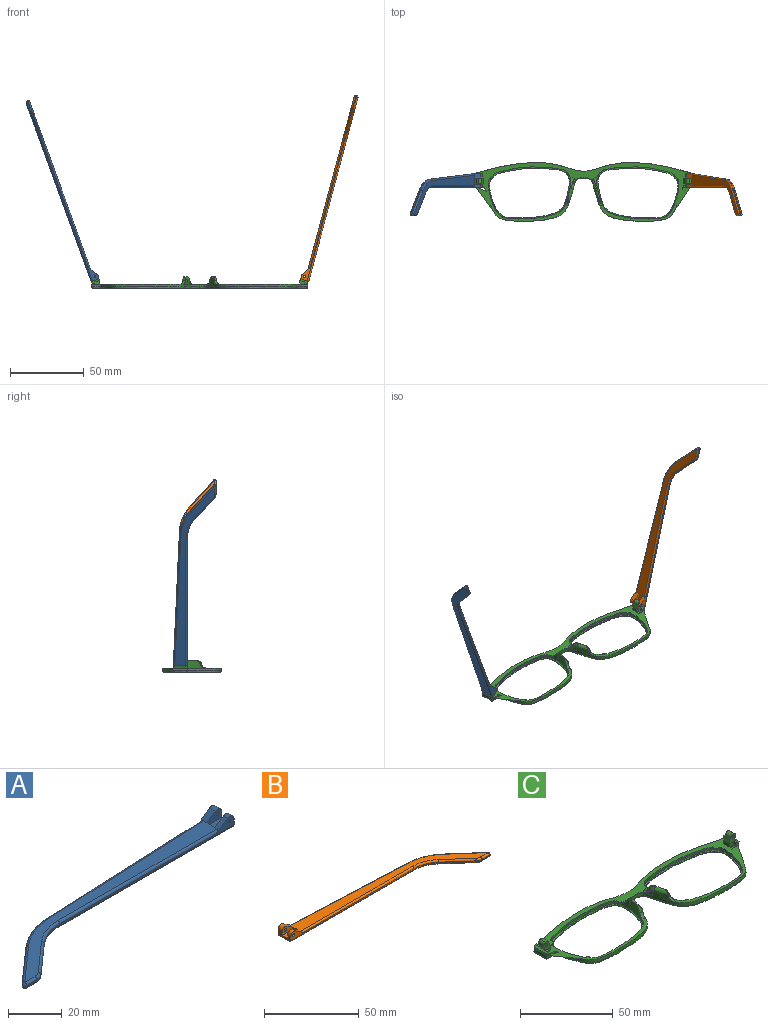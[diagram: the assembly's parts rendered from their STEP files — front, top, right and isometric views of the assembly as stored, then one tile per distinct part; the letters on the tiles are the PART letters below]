
ASSEMBLY  parts=3 mates=2
PART A: 43 faces, bbox 130.2x29.5x5.9 mm
  f0: plane 9.62x3.72mm, normal (1,0,0), area 24.7mm2, adj f1,f3,f4,f5,f10,f16,f18,f28
  f1: cylinder r=2.2mm len=3.45mm, axis (0,-1,0), area 11mm2, adj f0,f2,f4,f37
  f2: plane 6.01x3.91mm, normal (-0.55,0,0.84), area 12.7mm2, adj f1,f4,f9,f19,f37
  f3: plane 2.26x0.1mm, normal (0,0,1), area 0.1mm2, adj f0,f5,f18
  f4: plane 92.1x4.9mm, normal (0,-1,0), area 79.9mm2, adj f0,f1,f2,f14,f19,f36,f42
  f5: plane 93.42x4.13mm, normal (-0.04,1,0), area 64.8mm2, adj f0,f3,f11,f15,f17,f27,f28
  f6: plane 17.82x15.72mm, normal (-0.66,0.75,0), area 14.3mm2, adj f11,f12,f25,f30
  f7: plane 5.46x0.6mm, normal (0,-1,0), area 3.3mm2, adj f12,f13,f23,f32
  f8: plane 14.99x13.23mm, normal (0.66,-0.75,0), area 12mm2, adj f13,f14,f21,f34
  f9: plane 121.18x26.73mm, normal (0,0,1), area 627.7mm2, adj f2,f17,f19,f20,f21,f22,f23,f25
  f10: plane 129.1x27.08mm, normal (0,0,-1), area 686.5mm2, adj f0,f28,f29,f30,f32,f33,f34,f35
  f11: cylinder r=30mm len=18.52mm, axis (0,0,-1), area 12.2mm2, adj f5,f6,f26,f29
  f12: cylinder r=1mm len=1.75mm, axis (0,0,-1), area 1.5mm2, adj f6,f7,f24,f31
  f13: cylinder r=5mm len=3.31mm, axis (0,0,-1), area 2.2mm2, adj f7,f8,f22,f33
  f14: cylinder r=20mm len=13.23mm, axis (0,0,1), area 8.7mm2, adj f4,f8,f20,f35
  f15: plane 5.66x0.25mm, normal (0,0,-1), area 0.7mm2, adj f5,f17,f18
  f16: cylinder r=2.2mm len=3.45mm, axis (0,-1,0), area 14.8mm2, adj f0,f17,f18,f38
  f17: plane 6.01x3.91mm, normal (-0.55,0,0.84), area 16.9mm2, adj f5,f9,f15,f16,f18,f27,f38
  f18: plane 7.92x3.3mm, normal (0,1,0), area 15.9mm2, adj f0,f3,f15,f16,f17,f41
  f19: cylinder r=1mm len=84.18mm, axis (-1,0,0), area 131.4mm2, adj f2,f4,f9,f20
  f20: torus R=21mm, axis (0,0,1), area 23.1mm2, adj f9,f14,f19,f21
  f21: cylinder r=1mm len=15.65mm, axis (-0.75,-0.66,0), area 31.4mm2, adj f8,f9,f20,f22
  f22: torus R=4mm, axis (0,0,1), area 5.3mm2, adj f9,f13,f21,f23
  f23: cylinder r=1mm len=5.46mm, axis (-1,0,0), area 8.6mm2, adj f7,f9,f22,f24
  f24: sphere r=1mm, area 2.4mm2, adj f12,f23,f25
  f25: cylinder r=1mm len=18.48mm, axis (0.75,0.66,0), area 37.3mm2, adj f6,f9,f24,f26
  f26: torus R=29mm, axis (0,0,1), area 31.6mm2, adj f9,f11,f25,f27
  f27: cylinder r=1mm len=85.5mm, axis (1,0.04,0), area 133.5mm2, adj f5,f9,f17,f26
  f28: cylinder r=1mm len=93.46mm, axis (-1,-0.04,0), area 146.9mm2, adj f0,f5,f10,f29
  f29: torus R=29mm, axis (0,0,1), area 31.6mm2, adj f10,f11,f28,f30
  f30: cylinder r=1mm len=18.48mm, axis (-0.75,-0.66,0), area 37.3mm2, adj f6,f10,f29,f31
  f31: sphere r=1mm, area 2.4mm2, adj f12,f30,f32
  f32: cylinder r=1mm len=5.46mm, axis (1,0,0), area 8.6mm2, adj f7,f10,f31,f33
  f33: torus R=4mm, axis (0,0,1), area 5.3mm2, adj f10,f13,f32,f34
  f34: cylinder r=1mm len=15.65mm, axis (0.75,0.66,0), area 31.4mm2, adj f8,f10,f33,f35
  f35: torus R=21mm, axis (0,0,1), area 23.1mm2, adj f10,f14,f34,f36
  f36: cylinder r=1mm len=92.1mm, axis (1,0,0), area 144.7mm2, adj f0,f4,f10,f35
  f37: plane 7.92x4.7mm, normal (0,1,0), area 27mm2, adj f0,f1,f2,f39,f40,f42
  f38: plane 7.92x4.7mm, normal (0,-1,0), area 27mm2, adj f0,f16,f17,f39,f40,f41
  f39: plane 7.92x4.1mm, normal (0,0,1), area 32.5mm2, adj f0,f37,f38,f40
  f40: plane 4.1x1.4mm, normal (1,0,0), area 5.7mm2, adj f9,f37,f38,f39
  f41: cylinder r=0.5mm len=3.1mm, axis (0,-1,0), area 9.7mm2, adj f18,f38
  f42: cylinder r=0.5mm len=2.3mm, axis (0,-1,0), area 7.2mm2, adj f4,f37
PART B: 43 faces, bbox 130.2x29.5x5.9 mm
  f0: plane 9.62x3.72mm, normal (-1,0,0), area 24.7mm2, adj f1,f3,f4,f5,f10,f16,f18,f28
  f1: cylinder r=2.2mm len=3.45mm, axis (0,-1,0), area 11mm2, adj f0,f2,f4,f37
  f2: plane 6.01x3.91mm, normal (0.55,0,0.84), area 12.7mm2, adj f1,f4,f9,f19,f37
  f3: plane 2.26x0.1mm, normal (0,0,1), area 0.1mm2, adj f0,f5,f18
  f4: plane 92.1x4.9mm, normal (0,-1,0), area 78.2mm2, adj f0,f1,f2,f14,f19,f36,f42
  f5: plane 93.42x4.13mm, normal (0.04,1,0), area 64.8mm2, adj f0,f3,f11,f15,f17,f27,f28
  f6: plane 17.82x15.72mm, normal (0.66,0.75,0), area 14.3mm2, adj f11,f12,f25,f30
  f7: plane 5.46x0.6mm, normal (0,-1,0), area 3.3mm2, adj f12,f13,f23,f32
  f8: plane 14.99x13.23mm, normal (-0.66,-0.75,0), area 12mm2, adj f13,f14,f21,f34
  f9: plane 121.18x26.73mm, normal (0,0,1), area 627.7mm2, adj f2,f17,f19,f20,f21,f22,f23,f25
  f10: plane 129.1x27.08mm, normal (0,0,-1), area 686.5mm2, adj f0,f28,f29,f30,f32,f33,f34,f35
  f11: cylinder r=30mm len=18.52mm, axis (0,0,-1), area 12.2mm2, adj f5,f6,f26,f29
  f12: cylinder r=1mm len=1.75mm, axis (0,0,-1), area 1.5mm2, adj f6,f7,f24,f31
  f13: cylinder r=5mm len=3.31mm, axis (0,0,-1), area 2.2mm2, adj f7,f8,f22,f33
  f14: cylinder r=20mm len=13.23mm, axis (0,0,1), area 8.7mm2, adj f4,f8,f20,f35
  f15: plane 5.66x0.25mm, normal (0,0,-1), area 0.7mm2, adj f5,f17,f18
  f16: cylinder r=2.2mm len=3.45mm, axis (0,-1,0), area 14.8mm2, adj f0,f17,f18,f38
  f17: plane 6.01x3.91mm, normal (0.55,0,0.84), area 16.9mm2, adj f5,f9,f15,f16,f18,f27,f38
  f18: plane 7.92x3.3mm, normal (0,1,0), area 14.3mm2, adj f0,f3,f15,f16,f17,f41
  f19: cylinder r=1mm len=84.18mm, axis (1,0,0), area 131.4mm2, adj f2,f4,f9,f20
  f20: torus R=21mm, axis (0,0,1), area 23.1mm2, adj f9,f14,f19,f21
  f21: cylinder r=1mm len=15.65mm, axis (0.75,-0.66,0), area 31.4mm2, adj f8,f9,f20,f22
  f22: torus R=4mm, axis (0,0,1), area 5.3mm2, adj f9,f13,f21,f23
  f23: cylinder r=1mm len=5.46mm, axis (1,0,0), area 8.6mm2, adj f7,f9,f22,f24
  f24: sphere r=1mm, area 2.4mm2, adj f12,f23,f25
  f25: cylinder r=1mm len=18.48mm, axis (-0.75,0.66,0), area 37.3mm2, adj f6,f9,f24,f26
  f26: torus R=29mm, axis (0,0,1), area 31.6mm2, adj f9,f11,f25,f27
  f27: cylinder r=1mm len=85.5mm, axis (-1,0.04,0), area 133.5mm2, adj f5,f9,f17,f26
  f28: cylinder r=1mm len=93.46mm, axis (1,-0.04,0), area 146.9mm2, adj f0,f5,f10,f29
  f29: torus R=29mm, axis (0,0,1), area 31.6mm2, adj f10,f11,f28,f30
  f30: cylinder r=1mm len=18.48mm, axis (0.75,-0.66,0), area 37.3mm2, adj f6,f10,f29,f31
  f31: sphere r=1mm, area 2.4mm2, adj f12,f30,f32
  f32: cylinder r=1mm len=5.46mm, axis (-1,0,0), area 8.6mm2, adj f7,f10,f31,f33
  f33: torus R=4mm, axis (0,0,1), area 5.3mm2, adj f10,f13,f32,f34
  f34: cylinder r=1mm len=15.65mm, axis (-0.75,0.66,0), area 31.4mm2, adj f8,f10,f33,f35
  f35: torus R=21mm, axis (0,0,1), area 23.1mm2, adj f10,f14,f34,f36
  f36: cylinder r=1mm len=92.1mm, axis (-1,0,0), area 144.7mm2, adj f0,f4,f10,f35
  f37: plane 7.92x4.7mm, normal (0,1,0), area 25.4mm2, adj f0,f1,f2,f39,f40,f42
  f38: plane 7.92x4.7mm, normal (0,-1,0), area 25.4mm2, adj f0,f16,f17,f39,f40,f41
  f39: plane 7.92x4.1mm, normal (0,0,1), area 32.5mm2, adj f0,f37,f38,f40
  f40: plane 4.1x1.4mm, normal (-1,0,0), area 5.7mm2, adj f9,f37,f38,f39
  f41: cylinder r=0.88mm len=3.1mm, axis (0,-1,0), area 17mm2, adj f18,f38
  f42: cylinder r=0.88mm len=2.3mm, axis (0,-1,0), area 12.6mm2, adj f4,f37
PART C: 118 faces, bbox 148.1x41x17.9 mm
  f0: bspline ~1.82x1.22mm, area 0.7mm2, adj f1,f114,f116,f117
  f1: bspline ~2.66x2.04mm, area 1.9mm2, adj f0,f2,f113,f114,f117
  f2: bspline ~3.55x3.47mm, area 3.7mm2, adj f1,f3,f112,f113,f117
  f3: plane 147.69x40.6mm, normal (0,0,1), area 854.2mm2, adj f2,f4,f16,f17,f18,f19,f20,f21
  f4: plane 1.23x0.04mm, normal (0,0,1), area 0mm2, adj f3,f5,f114
  f5: plane 2.76x2.53mm, normal (0,-1,0), area 3.9mm2, adj f4,f6,f15,f16,f24
  f6: plane 9.65x1.24mm, normal (0,0,1), area 8.2mm2, adj f5,f7,f14,f15,f19,f20,f21,f24
  f7: plane 5.77x5.06mm, normal (0,-1,0), area 17mm2, adj f6,f8,f9,f11,f12,f13,f14,f23
  f8: cylinder r=1.98mm len=4mm, axis (0,-1,0), area 12.4mm2, adj f7,f12,f14,f21
  f9: plane 4x3.31mm, normal (-0.94,0,0.34), area 14.1mm2, adj f7,f10,f11,f21
  f10: plane 4x0.02mm, normal (0.34,0,0.94), area 0.1mm2, adj f9,f21,f22
  f11: cylinder r=1.98mm len=4mm, axis (0,1,0), area 12.4mm2, adj f7,f9,f12,f21
  f12: plane 4x0.01mm, normal (0.34,0,0.94), area 0mm2, adj f7,f8,f11,f21
  f13: cylinder r=0.88mm len=4mm, axis (0,-1,0), area 22mm2, adj f7,f21
  f14: plane 4x2.21mm, normal (0.94,0,-0.34), area 9.4mm2, adj f6,f7,f8,f21
  f15: plane 9.71x1.44mm, normal (0.34,0,0.94), area 13.9mm2, adj f5,f6,f16,f17,f18,f19
  f16: cone r=1mm half-angle=20deg, axis (0,0,1), area 2.3mm2, adj f3,f5,f15,f17
  f17: plane 7.67x1.6mm, normal (0.94,0,-0.34), area 13mm2, adj f3,f15,f16,f18
  f18: cylinder r=1mm len=2.28mm, axis (-0.34,0,-0.94), area 3mm2, adj f3,f15,f17,f19
  f19: plane 2.1x1.69mm, normal (0,1,0), area 2.8mm2, adj f3,f6,f15,f18,f20
  f20: plane 3.3x2.1mm, normal (-1,0,0), area 6.9mm2, adj f3,f6,f19,f21
  f21: plane 6.97x5.07mm, normal (0,1,0), area 22.7mm2, adj f3,f6,f8,f9,f10,f11,f12,f13
  f22: plane 4x2.36mm, normal (-1,0,0), area 9.5mm2, adj f3,f10,f21,f23
  f23: plane 3.2x2.36mm, normal (0,-1,0), area 5.7mm2, adj f3,f7,f22,f24
  f24: plane 2.35x2.1mm, normal (-1,0,0), area 4.9mm2, adj f3,f5,f6,f7,f23
  f25: bspline ~3.7x3.66mm, area 7.8mm2, adj f3,f26,f31,f39,f114
  f26: bspline ~7.26x7.26mm, area 6.3mm2, adj f25,f27,f31,f39
  f27: bspline ~10.27x4.83mm, area 21.4mm2, adj f26,f28,f31,f39,f114,f117
  f28: plane 3.63x0.97mm, normal (0,0,1), area 0.3mm2, adj f27,f29,f39
  f29: bspline ~15.5x15.35mm, area 6.4mm2, adj f28,f30,f39,f112,f117
  f30: extruded ~4.98x1.37mm, area 6.6mm2, adj f29,f39
  f31: extruded ~4.44x3.32mm, area 15.1mm2, adj f25,f26,f27,f32,f114
  f32: plane 4.46x1.45mm, normal (0,0,1), area 0.1mm2, adj f31,f114
  f33: cylinder r=1.3mm len=1.78mm, axis (0,0,1), area 1.3mm2, adj f3,f34,f39
  f34: plane 1.79x1.31mm, normal (0,0,-1), area 0.9mm2, adj f33,f39
  f35: cylinder r=1.3mm len=1.93mm, axis (0,0,1), area 1.5mm2, adj f3,f36,f39
  f36: plane 1.95x1.68mm, normal (0,0,-1), area 1.5mm2, adj f35,f39
  f37: cylinder r=2.28mm len=3.13mm, axis (0,0,1), area 2.5mm2, adj f3,f38,f39
  f38: plane 3.14x2.79mm, normal (0,0,-1), area 3.9mm2, adj f37,f39
  f39: extruded ~55.69x35.36mm, area 226.3mm2, adj f3,f25,f26,f27,f28,f29,f30,f33
  f40: extruded ~55.69x35.36mm, area 160.5mm2, adj f39,f41
  f41: plane 56.06x35.45mm, normal (0,0,1), area 126.1mm2, adj f40,f42
  f42: bspline ~56.14x35.88mm, area 235.6mm2, adj f41,f43,f58
  f43: bspline ~72.96x30.43mm, area 161.5mm2, adj f42,f44,f57,f58,f114
  f44: bspline ~72.96x30.43mm, area 161.5mm2, adj f43,f45,f48,f58,f109
  f45: bspline ~56.14x35.88mm, area 235.6mm2, adj f44,f46,f58
  f46: plane 56.06x35.45mm, normal (0,0,1), area 126.1mm2, adj f45,f47
  f47: extruded ~55.69x35.36mm, area 160.5mm2, adj f46,f86
  f48: bspline ~1x1mm, area 0.8mm2, adj f44,f49,f109
  f49: bspline ~8.97x1.23mm, area 12.6mm2, adj f48,f50,f58,f109
  f50: bspline ~1.04x1mm, area 0.7mm2, adj f49,f51,f109
  f51: bspline ~45.82x8.59mm, area 59.8mm2, adj f50,f52,f58,f109
  f52: bspline ~37.02x6.7mm, area 56.6mm2, adj f51,f53,f58,f110
  f53: bspline ~37.02x6.7mm, area 56.6mm2, adj f52,f54,f58,f111
  f54: bspline ~45.82x8.59mm, area 59.8mm2, adj f53,f55,f58,f114
  f55: bspline ~1.04x1mm, area 0.8mm2, adj f54,f56,f114
  f56: bspline ~8.97x1.23mm, area 12.6mm2, adj f55,f57,f58,f114
  f57: bspline ~1x1mm, area 0.8mm2, adj f43,f56,f114
  f58: plane 144.78x37.9mm, normal (0,0,-1), area 565.6mm2, adj f42,f43,f44,f45,f49,f51,f52,f53
  f59: plane 3.19x1.37mm, normal (0,0,-1), area 2.1mm2, adj f39,f60
  f60: cylinder r=2.28mm len=3.17mm, axis (0,0,1), area 2.1mm2, adj f3,f39,f59,f112
  f61: bspline ~6.38x2.14mm, area 2.6mm2, adj f3,f62,f113,f114
  f62: bspline ~6.38x2.14mm, area 2.6mm2, adj f3,f61,f63,f109
  f63: bspline ~2.1x1.46mm, area 0.6mm2, adj f62,f64,f76,f109
  f64: bspline ~2.65x2.03mm, area 1.9mm2, adj f63,f65,f68,f76,f109
  f65: bspline ~2.19x1.4mm, area 0.7mm2, adj f64,f66,f68,f109
  f66: extruded ~3.67x3.11mm, area 5.9mm2, adj f65,f67,f68,f109
  f67: bspline ~5.24x1.75mm, area 0mm2, adj f66,f109
  f68: bspline ~6.1x4.93mm, area 12.6mm2, adj f64,f65,f66,f69,f74,f76,f109
  f69: bspline ~10.27x4.83mm, area 21.5mm2, adj f68,f70,f71,f73,f86,f109
  f70: plane 3.63x0.97mm, normal (0,0,1), area 0.3mm2, adj f69,f74,f86
  f71: extruded ~4.44x3.32mm, area 15.1mm2, adj f69,f72,f73,f87,f109
  f72: plane 4.46x1.45mm, normal (0,0,1), area 0.1mm2, adj f71,f109
  f73: bspline ~7.26x7.26mm, area 6.2mm2, adj f69,f71,f86,f87
  f74: bspline ~15.5x15.35mm, area 6.4mm2, adj f68,f70,f75,f77,f86
  f75: extruded ~4.98x1.36mm, area 6.6mm2, adj f74,f86
  f76: bspline ~3.55x3.47mm, area 3.7mm2, adj f3,f63,f64,f68,f77
  f77: bspline ~5.94x4.42mm, area 7.9mm2, adj f3,f74,f76,f78,f86
  f78: cylinder r=2.28mm len=3.17mm, axis (0,0,1), area 2.1mm2, adj f3,f77,f79,f86
  f79: plane 3.19x1.37mm, normal (0,0,-1), area 2.1mm2, adj f78,f86
  f80: cylinder r=2.28mm len=3.13mm, axis (0,0,1), area 2.5mm2, adj f3,f81,f86
  f81: plane 3.14x2.79mm, normal (0,0,-1), area 3.9mm2, adj f80,f86
  f82: cylinder r=1.3mm len=1.93mm, axis (0,0,1), area 1.5mm2, adj f3,f83,f86
  f83: plane 1.95x1.68mm, normal (0,0,-1), area 1.5mm2, adj f82,f86
  f84: cylinder r=1.3mm len=1.78mm, axis (0,0,1), area 1.3mm2, adj f3,f85,f86
  f85: plane 1.79x1.31mm, normal (0,0,-1), area 0.9mm2, adj f84,f86
  f86: extruded ~55.69x35.36mm, area 226.4mm2, adj f3,f47,f69,f70,f73,f74,f75,f77
  f87: bspline ~3.7x3.66mm, area 7.8mm2, adj f3,f71,f73,f86,f109
  f88: plane 2.35x2.1mm, normal (1,0,0), area 4.9mm2, adj f3,f89,f91,f98,f100
  f89: plane 2.76x2.53mm, normal (0,-1,0), area 3.9mm2, adj f88,f90,f91,f107,f108
  f90: plane 9.71x1.44mm, normal (-0.34,0,0.94), area 13.9mm2, adj f89,f91,f104,f105,f106,f107
  f91: plane 9.65x1.24mm, normal (0,0,1), area 8.2mm2, adj f88,f89,f90,f92,f98,f102,f103,f104
  f92: plane 4x2.21mm, normal (-0.94,0,-0.34), area 9.4mm2, adj f91,f93,f98,f102
  f93: cylinder r=1.98mm len=4mm, axis (0,-1,0), area 12.4mm2, adj f92,f94,f98,f102
  f94: plane 4x0.01mm, normal (-0.34,0,0.94), area 0mm2, adj f93,f95,f98,f102
  f95: cylinder r=1.98mm len=4mm, axis (0,1,0), area 12.4mm2, adj f94,f96,f98,f102
  f96: plane 4x3.31mm, normal (0.94,0,0.34), area 14.1mm2, adj f95,f97,f98,f102
  f97: plane 4x0.02mm, normal (-0.34,0,0.94), area 0.1mm2, adj f96,f101,f102
  f98: plane 5.77x5.06mm, normal (0,-1,0), area 17mm2, adj f88,f91,f92,f93,f94,f95,f96,f99
  f99: cylinder r=0.88mm len=4mm, axis (0,-1,0), area 22mm2, adj f98,f102
  f100: plane 3.2x2.36mm, normal (0,-1,0), area 5.7mm2, adj f3,f88,f98,f101
  f101: plane 4x2.36mm, normal (1,0,0), area 9.5mm2, adj f3,f97,f100,f102
  f102: plane 6.97x5.07mm, normal (0,1,0), area 22.7mm2, adj f3,f91,f92,f93,f94,f95,f96,f97
  f103: plane 3.3x2.1mm, normal (1,0,0), area 6.9mm2, adj f3,f91,f102,f104
  f104: plane 2.1x1.69mm, normal (0,1,0), area 2.8mm2, adj f3,f90,f91,f103,f105
  f105: cylinder r=1mm len=2.28mm, axis (0.34,0,-0.94), area 3mm2, adj f3,f90,f104,f106
  f106: plane 7.67x1.6mm, normal (-0.94,0,-0.34), area 13mm2, adj f3,f90,f105,f107
  f107: cone r=1mm half-angle=20deg, axis (0,0,1), area 2.3mm2, adj f3,f89,f90,f106
  f108: plane 1.23x0.04mm, normal (0,0,1), area 0mm2, adj f3,f89,f109
  f109: extruded ~73.26x39.87mm, area 292.5mm2, adj f3,f44,f48,f49,f50,f51,f62,f63
  f110: extruded ~35.39x5.69mm, area 72.2mm2, adj f3,f52,f109,f111
  f111: extruded ~35.39x5.69mm, area 72.2mm2, adj f3,f53,f110,f114
  f112: bspline ~5.1x3.97mm, area 7.9mm2, adj f2,f3,f29,f39,f60
  f113: bspline ~2.1x1.46mm, area 0.6mm2, adj f1,f2,f61,f114
  f114: extruded ~73.26x39.87mm, area 292.5mm2, adj f0,f1,f3,f4,f25,f27,f31,f32
  f115: bspline ~5.24x1.75mm, area 0mm2, adj f114,f116
  f116: extruded ~3.67x3.11mm, area 5.9mm2, adj f0,f114,f115,f117
  f117: bspline ~6.1x4.93mm, area 12.7mm2, adj f0,f1,f2,f27,f29,f114,f116
PLACE A rot(axis=(0,1,0),70deg) t=(-84.77,-5.75,56)mm
PLACE B rot(axis=(0,-1,0),75deg) t=(68.2,-5.75,-61.61)mm
PLACE C t=(10.15,-1.13,-5.77)mm
MATE revolute A.f1 <-> C.f95  axis (0,-1,0) through (-60.89,2.72,1.22)mm
MATE revolute B.f41 <-> C.f8  axis (0,-1,0) through (81.2,2.72,1.21)mm
